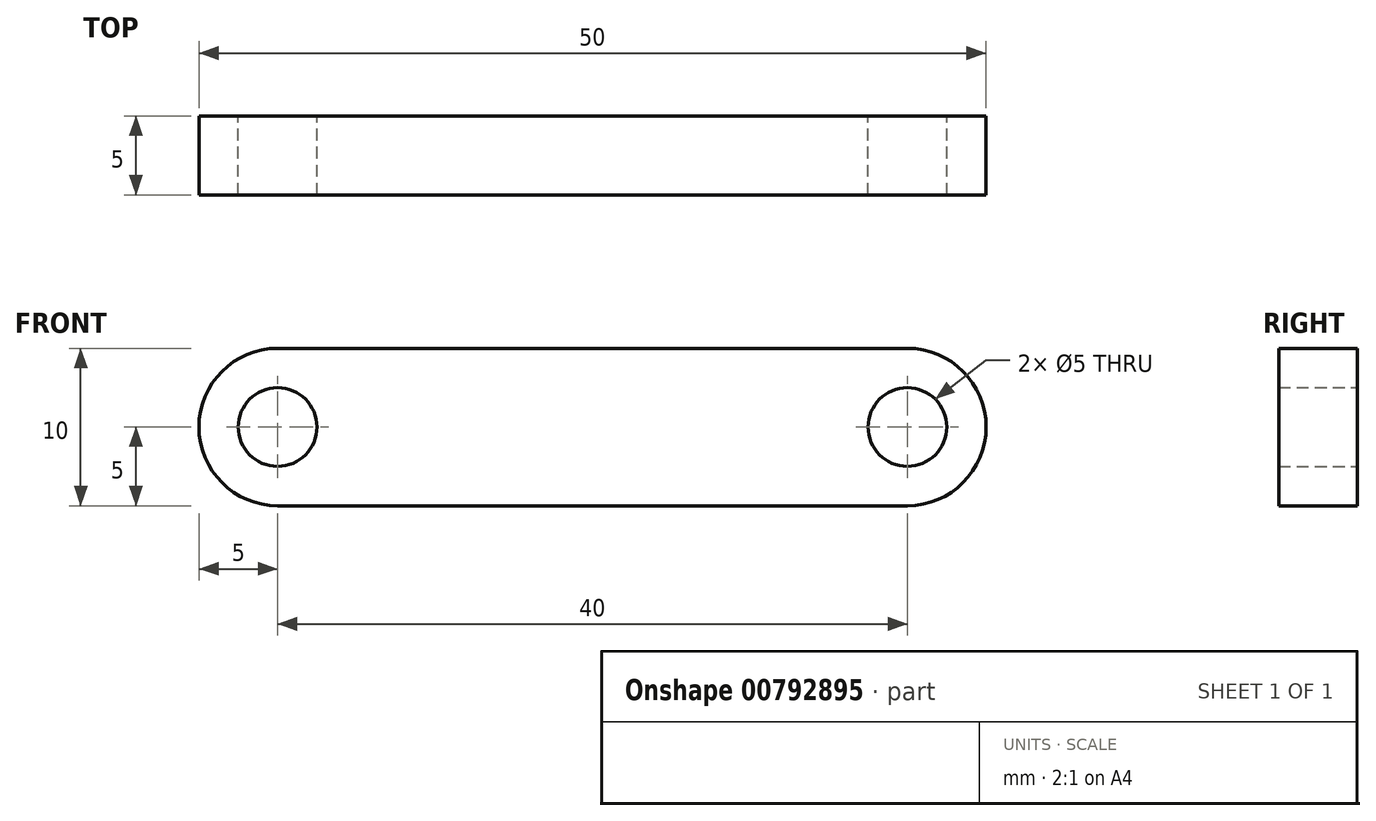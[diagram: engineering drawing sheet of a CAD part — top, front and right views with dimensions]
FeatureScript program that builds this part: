
annotation { "Feature Type Name" : "Feature", "Feature Type Description" : "" }
export const myFeature = defineFeature(function(context is Context, id is Id, definition is map)
    precondition{}
    {
        {
            var Q0;
            Q0=qCreatedBy(makeId("Front.planeOp"),FACE);
            var sketch = newSketch(context, id + "F0", { "sketchPlane" : qUnion([Q0])});
            skCircle(sketch, "E0", {"center": v(0, 0) * mm, "radius": 2.5 * mm});
            skArc(sketch, "E1", {"start": v(0, 5) * mm, "mid": v(-5, 0) * mm, "end": v(0, -5) * mm});
            skArc(sketch, "E2", {"start": v(40, -5) * mm, "mid": v(45, 0) * mm, "end": v(40, 5) * mm});
            skCircle(sketch, "E3", {"center": v(40, 0) * mm, "radius": 2.5 * mm});
            skLineSegment(sketch, "E4", {"start": v(0, 5) * mm, "end": v(40, 5) * mm});
            skLineSegment(sketch, "E5", {"start": v(40, -5) * mm, "end": v(0, -5) * mm});
            skSolve(sketch);
        }
        {
            var Q0;
            Q0=makeQuery(id+"F0.imprint","IMPRINT",FACE,{"disambiguationData":[TD([[makeQuery(id+"F0.imprint","IMPRINT",EDGE,{"derivedFrom":sQuery(id+"F0.wireOp",EDGE,"E0")}),-1.0]])]});
            extrude(context, id + "F1", {"entities" : qUnion([Q0]), "depth" : 5 * mm, "offsetDistance" : 25 * mm});
        }
    });
